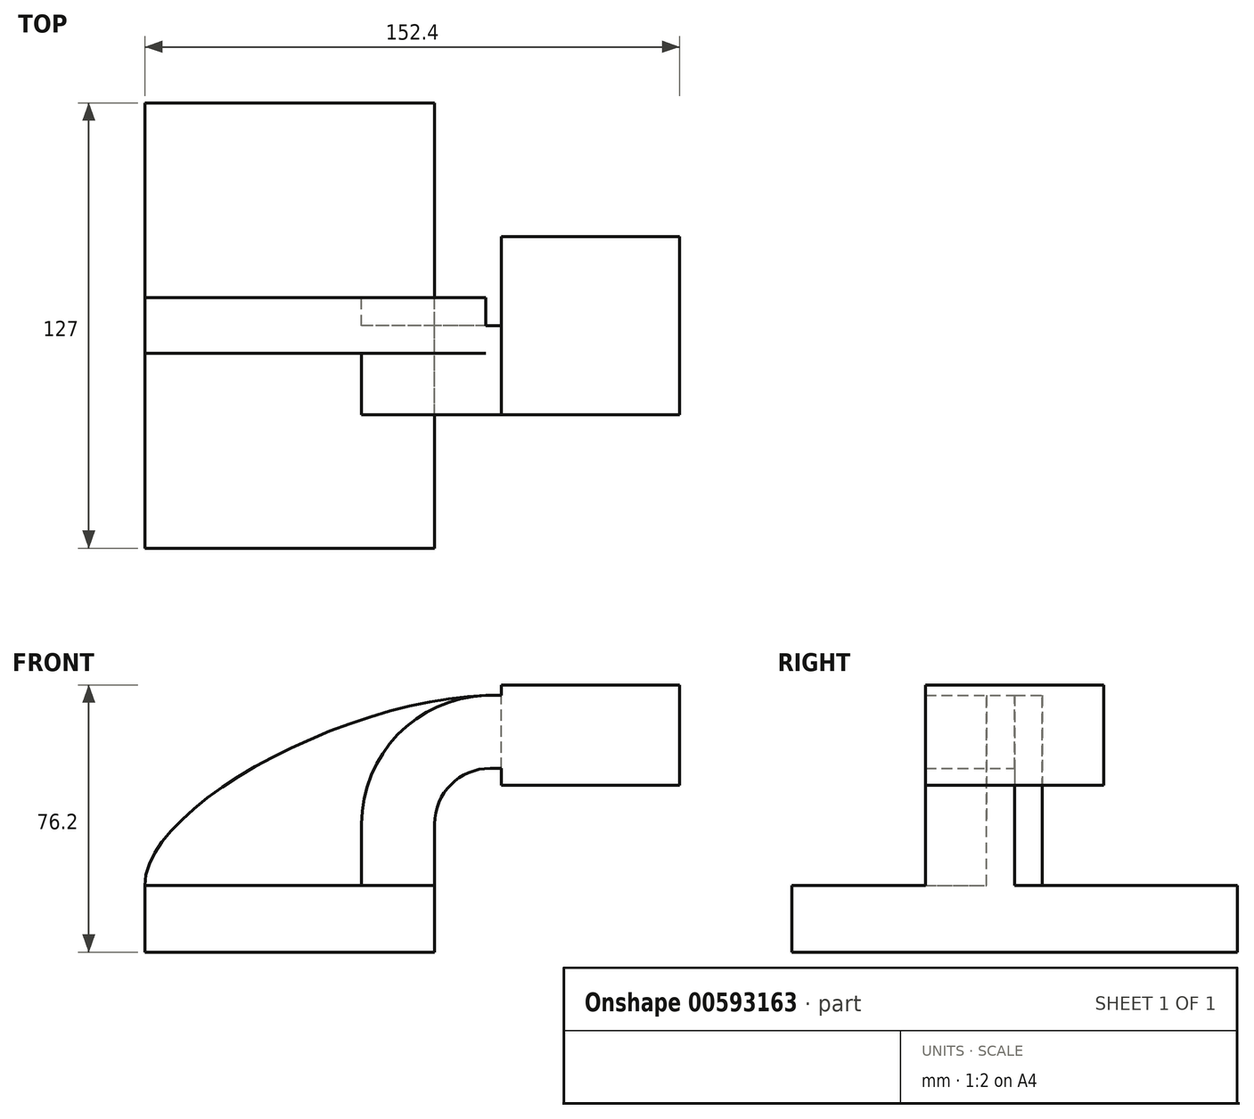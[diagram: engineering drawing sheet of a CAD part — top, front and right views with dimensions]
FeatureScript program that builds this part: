
annotation { "Feature Type Name" : "Feature", "Feature Type Description" : "" }
export const myFeature = defineFeature(function(context is Context, id is Id, definition is map)
    precondition{}
    {
        {
            var Q0;
            Q0=qCreatedBy(makeId("Front.planeOp"),FACE);
            var sketch = newSketch(context, id + "F0", { "sketchPlane" : qUnion([Q0])});
            skLineSegment(sketch, "E0.bottom", {"start": v(41.28, 9.53) * mm, "end": v(-41.28, 9.52) * mm});
            skLineSegment(sketch, "E0.top", {"start": v(41.28, -9.52) * mm, "end": v(-41.28, -9.53) * mm});
            skLineSegment(sketch, "E0.left", {"start": v(41.28, 9.53) * mm, "end": v(41.28, -9.52) * mm});
            skLineSegment(sketch, "E0.right", {"start": v(-41.28, 9.52) * mm, "end": v(-41.28, -9.53) * mm});
            skPoint(sketch, "E0.middle", {"position": v(0, 0) * mm});
            skLineSegment(sketch, "E1.bottom", {"start": v(111.12, 38.1) * mm, "end": v(60.33, 38.1) * mm});
            skLineSegment(sketch, "E1.top", {"start": v(111.12, 66.68) * mm, "end": v(60.33, 66.68) * mm});
            skLineSegment(sketch, "E1.left", {"start": v(111.12, 38.1) * mm, "end": v(111.12, 66.68) * mm});
            skLineSegment(sketch, "E1.right", {"start": v(60.33, 38.1) * mm, "end": v(60.33, 66.68) * mm});
            skPoint(sketch, "E1.middle", {"position": v(85.72, 52.39) * mm});
            skLineSegment(sketch, "E2", {"start": v(41.28, 9.53) * mm, "end": v(41.28, 27) * mm});
            skArc(sketch, "E3", {"start": v(41.28, 27) * mm, "mid": v(45.92, 38.23) * mm, "end": v(57.15, 42.88) * mm});
            skLineSegment(sketch, "E4", {"start": v(57.15, 42.88) * mm, "end": v(85.72, 42.88) * mm});
            skLineSegment(sketch, "E5.0", {"start": v(57.15, 63.67) * mm, "end": v(85.72, 63.67) * mm});
            skArc(sketch, "E5.1", {"start": v(20.48, 27) * mm, "mid": v(31.22, 52.93) * mm, "end": v(57.15, 63.67) * mm});
            skLineSegment(sketch, "E5.2", {"start": v(20.48, 9.53) * mm, "end": v(20.48, 27) * mm});
            skFitSpline(sketch, "E6", {"points": [v(-41.28, 9.53) * mm, v(57.15, 63.67) * mm], "startDerivative": vector(-0.23, 68.73) * mm, "endDerivative": vector(116.98, 1.05) * mm});
            skSolve(sketch);
        }
        {
            var Q0;
            Q0=makeQuery(id+"F0.imprint","IMPRINT",FACE,{"disambiguationData":[TD([[makeQuery(id+"F0.imprint","IMPRINT",EDGE,{"derivedFrom":sQuery(id+"F0.wireOp",EDGE,"E0.top")}),-1.0]])]});
            extrude(context, id + "F1", {"entities" : qUnion([Q0]), "endBound" : BoundingType.SYMMETRIC, "depth" : 127 * mm, "offsetDistance" : 25.4 * mm});
        }
        {
            var Q0;
            {var subQ1=sQuery(id+"F0.wireOp",EDGE,"E2");Q0=makeQuery(id+"F0.imprint","IMPRINT",FACE,{"disambiguationData":[TD([[makeQuery(id+"F0.imprint","IMPRINT",EDGE,{"derivedFrom":subQ1}),1.0]])]});}
            extrude(context, id + "F2", {"entities" : qUnion([Q0]), "operationType" : NewBodyOperationType.ADD, "depth" : 25.4 * mm, "offsetDistance" : 25.4 * mm});
        }
        {
            var Q0;
            {var subQ3=sQuery(id+"F0.wireOp",EDGE,"E5.2");Q0=makeQuery(id+"F0.imprint","IMPRINT",FACE,{"disambiguationData":[TD([[makeQuery(id+"F0.imprint","IMPRINT",EDGE,{"derivedFrom":subQ3}),1.0]])]});}
            extrude(context, id + "F3", {"entities" : qUnion([Q0]), "operationType" : NewBodyOperationType.ADD, "endBound" : BoundingType.SYMMETRIC, "depth" : 15.88 * mm, "offsetDistance" : 25.4 * mm});
        }
        {
            var Q0;
            {var subQ1=sQuery(id+"F0.wireOp",EDGE,"E1.bottom");Q0=makeQuery(id+"F0.imprint","IMPRINT",FACE,{"disambiguationData":[TD([[makeQuery(id+"F0.imprint","IMPRINT",EDGE,{"derivedFrom":subQ1}),-1.0]])]});}
            extrude(context, id + "F4", {"entities" : qUnion([Q0]), "operationType" : NewBodyOperationType.ADD, "endBound" : BoundingType.SYMMETRIC, "oppositeDirection" : true, "depth" : 50.8 * mm, "offsetDistance" : 25.4 * mm});
        }
    });
